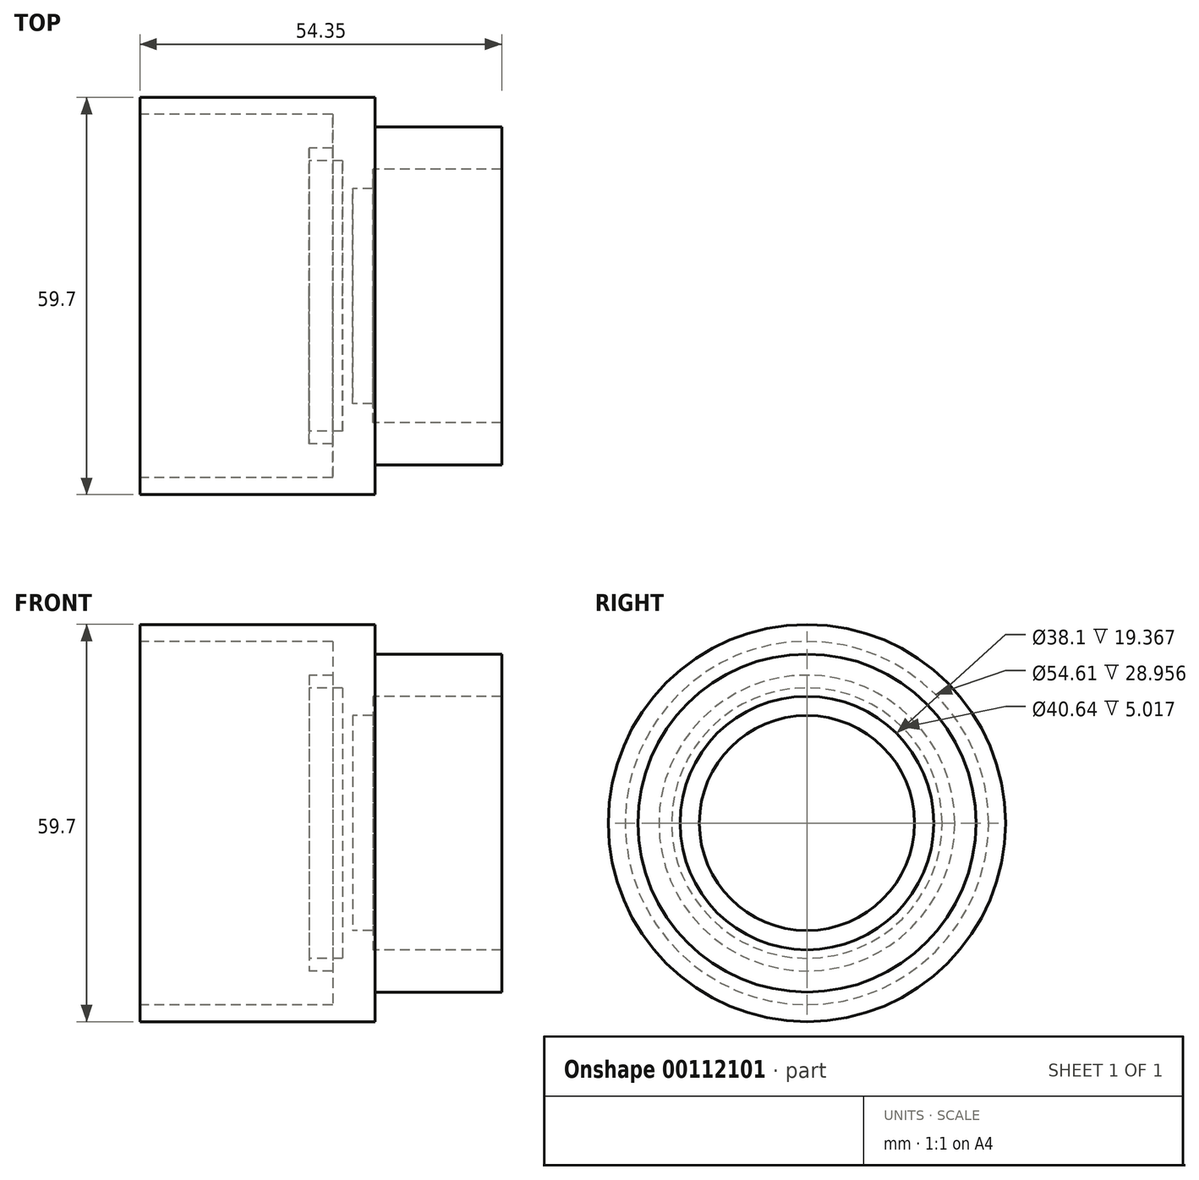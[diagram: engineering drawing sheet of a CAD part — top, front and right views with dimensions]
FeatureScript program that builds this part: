
annotation { "Feature Type Name" : "Feature", "Feature Type Description" : "" }
export const myFeature = defineFeature(function(context is Context, id is Id, definition is map)
    precondition{}
    {
        {
            var Q0;
            Q0=qCreatedBy(makeId("Top.planeOp"),FACE);
            var sketch = newSketch(context, id + "F0", { "sketchPlane" : qUnion([Q0])});
            skLineSegment(sketch, "E0", {"start": v(0, 0) * mm, "end": v(97.82, 0) * mm, "construction": true});
            skLineSegment(sketch, "E1", {"start": v(-17.52, 0) * mm, "end": v(-17.52, 20.32) * mm});
            skLineSegment(sketch, "E2", {"start": v(-17.52, 20.32) * mm, "end": v(-22.53, 20.32) * mm});
            skLineSegment(sketch, "E3", {"start": v(-22.53, 20.32) * mm, "end": v(-22.53, 22.23) * mm});
            skLineSegment(sketch, "E4", {"start": v(-22.53, 22.23) * mm, "end": v(-18.98, 22.23) * mm});
            skLineSegment(sketch, "E5", {"start": v(-18.98, 22.23) * mm, "end": v(-18.98, 27.3) * mm});
            skLineSegment(sketch, "E6", {"start": v(-18.98, 27.3) * mm, "end": v(-47.93, 27.3) * mm});
            skLineSegment(sketch, "E7", {"start": v(-47.93, 27.3) * mm, "end": v(-47.93, 29.84) * mm});
            skLineSegment(sketch, "E8", {"start": v(-47.93, 29.84) * mm, "end": v(-12.63, 29.85) * mm});
            skLineSegment(sketch, "E9", {"start": v(6.42, 25.4) * mm, "end": v(6.42, 19.05) * mm});
            skLineSegment(sketch, "E10", {"start": v(-12.94, 16.15) * mm, "end": v(-16, 16.15) * mm});
            skLineSegment(sketch, "E11", {"start": v(-16, 16.15) * mm, "end": v(-16, 0) * mm});
            skLineSegment(sketch, "E12", {"start": v(-17.52, 0) * mm, "end": v(-16, 0) * mm});
            skLineSegment(sketch, "E13", {"start": v(-12.94, 16.15) * mm, "end": v(-12.94, 19.05) * mm});
            skLineSegment(sketch, "E14", {"start": v(-12.94, 19.05) * mm, "end": v(6.42, 19.05) * mm});
            skLineSegment(sketch, "E15", {"start": v(-12.63, 29.85) * mm, "end": v(-12.63, 25.4) * mm});
            skLineSegment(sketch, "E16", {"start": v(-12.63, 25.4) * mm, "end": v(6.42, 25.4) * mm});
            skSolve(sketch);
        }
        {
            var Q0;
            Q0=makeQuery(id+"F0.imprint","IMPRINT",FACE,{"disambiguationData":[TD([[makeQuery(id+"F0.imprint","IMPRINT",EDGE,{"derivedFrom":sQuery(id+"F0.wireOp",EDGE,"E1")}),-1.0]])]});
            var Q1;
            Q1=sQuery(id+"F0.wireOp",EDGE,"E0");
            revolve(context, id + "F1", {"entities" : qUnion([Q0]), "axis" : qUnion([Q1]), "revolveType" : RevolveType.FULL});
        }
    });
